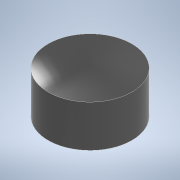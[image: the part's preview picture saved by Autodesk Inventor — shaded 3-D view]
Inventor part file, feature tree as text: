
AUTODESK INVENTOR PART (.ipt)
format: ipt  version: 2021 (Build 250183000, 183)  size: 124,416 bytes
history: native  units: mm
features: revolve x1, sketch x1
ambient origin geometry x8: Origin, YZ Plane, XZ Plane, XY Plane, X Axis, Y Axis, Z Axis, Center Point
bodies: Solid1 (feature_tree)
feature tree (2):
  revolve  "Revolution1"  [1 undecoded]
  sketch  "Sketch1"  dims[d0=20.0mm d1=23.0mm d2=0.0mm d3=21.0mm d5=25.0mm d6=90.0deg d7=23.0mm]
note: 1 required parameter value undecoded (feature->parameter linkage not recoverable at this tier; creation-order binding heuristic only, values carry confidence <= 0.55)
